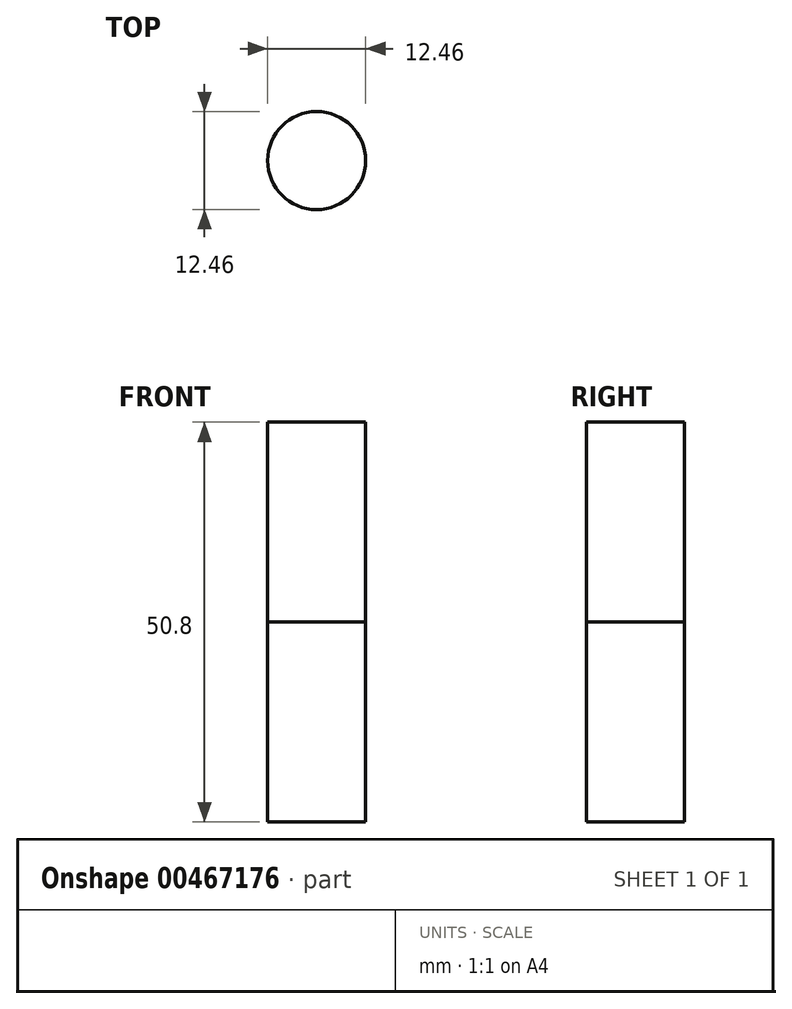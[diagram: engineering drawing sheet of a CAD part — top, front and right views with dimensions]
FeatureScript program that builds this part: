
annotation { "Feature Type Name" : "Feature", "Feature Type Description" : "" }
export const myFeature = defineFeature(function(context is Context, id is Id, definition is map)
    precondition{}
    {
        {
            var Q0;
            Q0=qCreatedBy(makeId("Front.planeOp"),FACE);
            var sketch = newSketch(context, id + "F0", { "sketchPlane" : qUnion([Q0])});
            skArc(sketch, "E0", {"start": v(0, 30.38) * mm, "mid": v(-36.06, -5.11) * mm, "end": v(0, -40.6) * mm});
            skLineSegment(sketch, "E1", {"start": v(0, 30.38) * mm, "end": v(0, -40.6) * mm});
            skSolve(sketch);
        }
        {
            var Q0;
            Q0=qCreatedBy(makeId("Top.planeOp"),FACE);
            var sketch = newSketch(context, id + "F1", { "sketchPlane" : qUnion([Q0])});
            skCircle(sketch, "E2", {"center": v(0, 0) * mm, "radius": 6.23 * mm});
            skSolve(sketch);
        }
        {
            var Q0;
            Q0 = qSketchRegion(id + "F1", true);
            extrude(context, id + "F2", {"entities" : qUnion([Q0]), "oppositeDirection" : true, "depth" : 25.4 * mm});
        }
        {
            var Q0;
            Q0=makeQuery(id+"F2.opExtrude","CAP_FACE",FACE,{"disambiguationData":[OSD([sQuery(id+"F1.wireOp",EDGE,"E2")])],"isStart":false});
            extrude(context, id + "F3", {"entities" : qUnion([Q0]), "depth" : 25.4 * mm});
        }
    });
